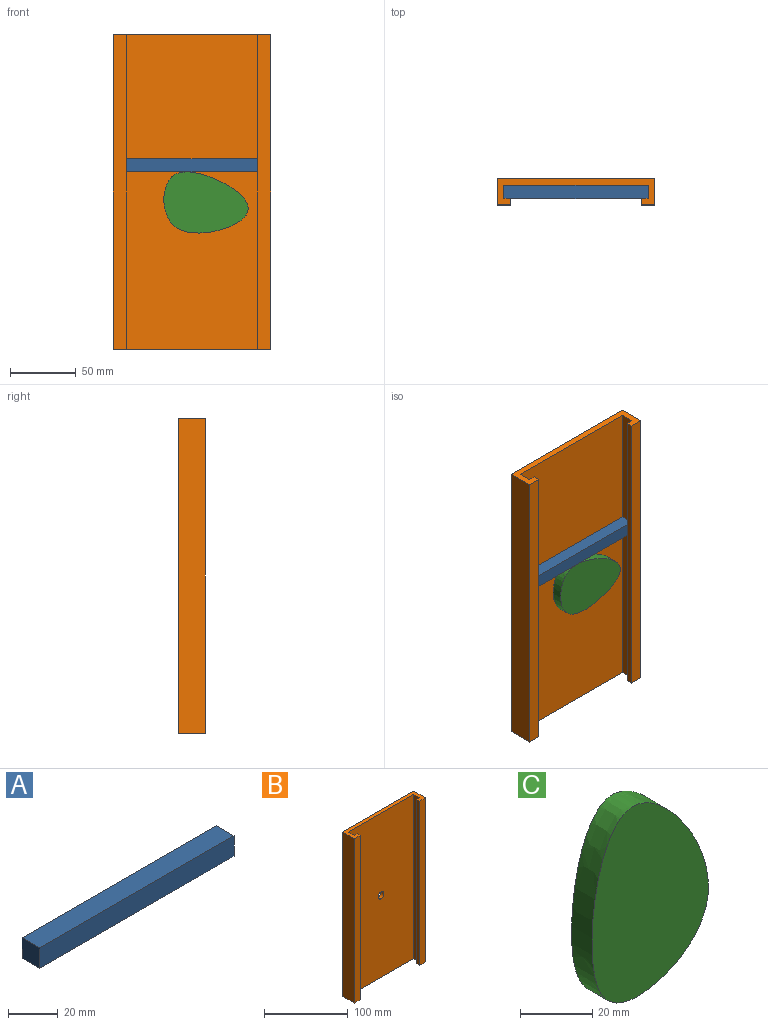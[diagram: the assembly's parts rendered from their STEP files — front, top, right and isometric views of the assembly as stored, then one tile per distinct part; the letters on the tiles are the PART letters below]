
ASSEMBLY  parts=3 mates=2
PART A: 6 faces, bbox 110x10x10 mm
  f0: plane 10x10mm, normal (1,0,0), area 100mm2, adj f1,f2,f4,f5
  f1: plane 110x10mm, normal (0,0,1), area 1100mm2, adj f0,f3,f4,f5
  f2: plane 110x10mm, normal (0,0,-1), area 1100mm2, adj f0,f3,f4,f5
  f3: plane 10x10mm, normal (-1,0,0), area 100mm2, adj f1,f2,f4,f5
  f4: plane 110x10mm, normal (0,1,0), area 1100mm2, adj f0,f1,f2,f3
  f5: plane 110x10mm, normal (0,-1,0), area 1100mm2, adj f0,f1,f2,f3
PART B: 15 faces, bbox 120x20x240 mm
  f0: plane 240x5mm, normal (1,0,0), area 1200mm2, adj f1,f3,f8,f13
  f1: plane 120x20mm, normal (0,0,-1), area 800mm2, adj f0,f2,f4,f5,f6,f7,f8,f9
  f2: plane 240x5mm, normal (-1,0,0), area 1200mm2, adj f1,f3,f6,f11
  f3: plane 120x20mm, normal (0,0,1), area 800mm2, adj f0,f2,f4,f5,f6,f7,f8,f9
  f4: plane 240x110mm, normal (0,-1,0), area 26321.5mm2, adj f1,f3,f5,f7,f14
  f5: plane 240x10mm, normal (-1,0,0), area 2400mm2, adj f1,f3,f4,f6
  f6: plane 240x5mm, normal (0,1,0), area 1200mm2, adj f1,f2,f3,f5
  f7: plane 240x10mm, normal (1,0,0), area 2400mm2, adj f1,f3,f4,f8
  f8: plane 240x5mm, normal (0,1,0), area 1200mm2, adj f0,f1,f3,f7
  f9: plane 240x120mm, normal (0,1,0), area 28721.5mm2, adj f1,f3,f10,f12,f14
  f10: plane 240x20mm, normal (1,0,0), area 4800mm2, adj f1,f3,f9,f11
  f11: plane 240x10mm, normal (0,-1,0), area 2400mm2, adj f1,f2,f3,f10
  f12: plane 240x20mm, normal (-1,0,0), area 4800mm2, adj f1,f3,f9,f13
  f13: plane 240x10mm, normal (0,-1,0), area 2400mm2, adj f0,f1,f3,f12
  f14: cylinder r=5mm len=10mm, axis (0,-1,0), area 157.1mm2, adj f4,f9
PART C: 5 faces, bbox 51x15x69 mm
  f0: plane 10x10mm, normal (0,1,0), area 78.5mm2, adj f1
  f1: cylinder r=5mm len=10mm, axis (0,-1,0), area 219.9mm2, adj f0,f4
  f2: extruded ~65.1x45.46mm, area 1405.8mm2, adj f3,f4
  f3: plane 69.02x51.05mm, normal (0,-1,0), area 2271.9mm2, adj f2
  f4: plane 69.02x51.05mm, normal (0,1,0), area 2193.4mm2, adj f1,f2
PLACE A t=(0,0,-94.69)mm
PLACE B at identity fixed
PLACE C rot(axis=(0,1,0),108.7deg) t=(-38.41,0,-113.69)mm
MATE revolute B.f14 <-> C.f1  axis (0,1,0) through (0,7,0)mm
MATE slider B.f3 <-> A.f1  axis (0,0,1) through (-55,2,120)mm
